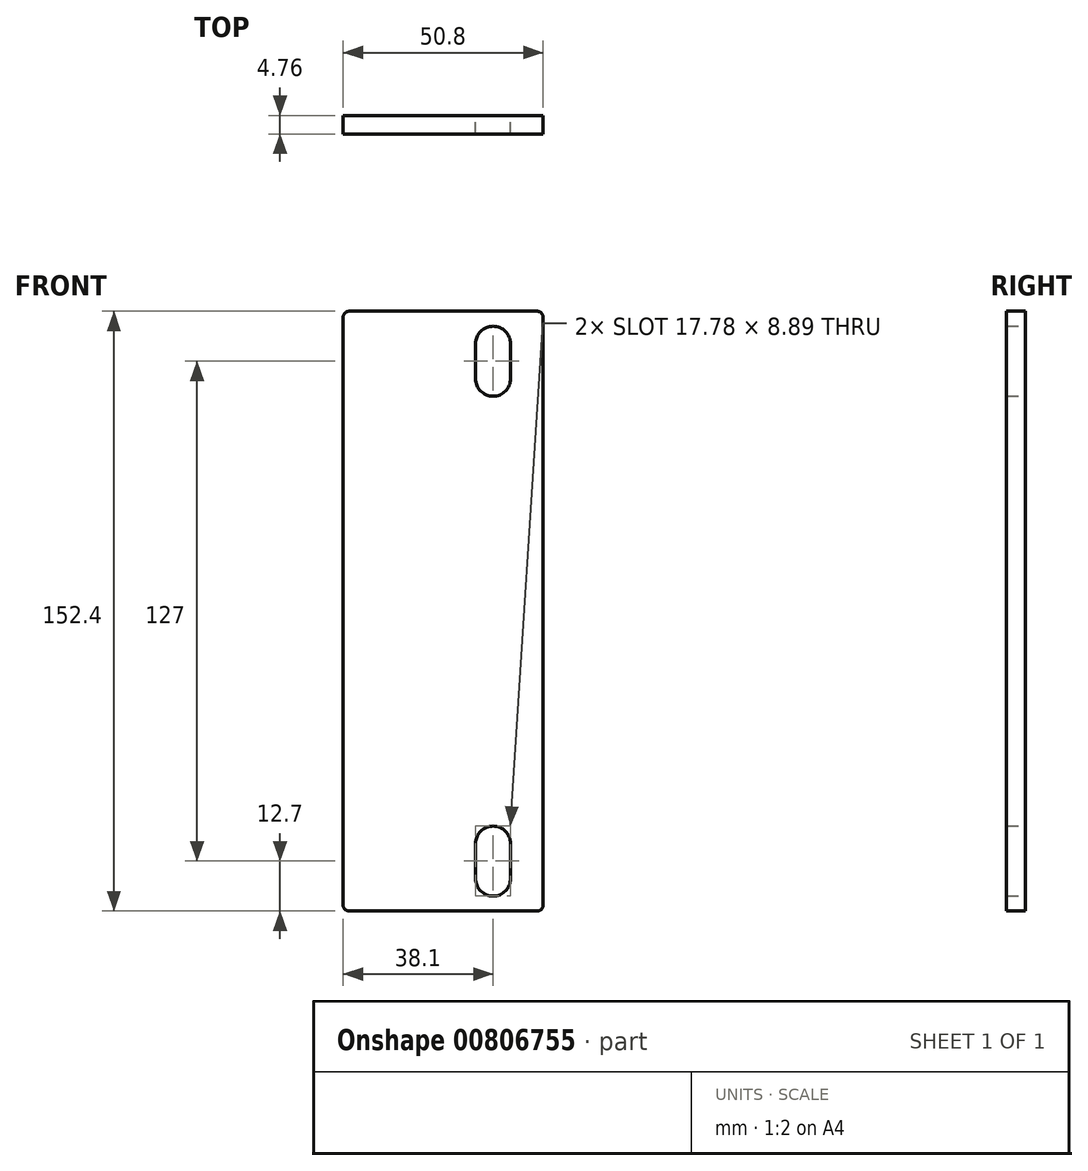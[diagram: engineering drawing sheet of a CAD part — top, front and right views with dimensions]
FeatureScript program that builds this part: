
annotation { "Feature Type Name" : "Feature", "Feature Type Description" : "" }
export const myFeature = defineFeature(function(context is Context, id is Id, definition is map)
    precondition{}
    {
        {
            var Q0;
            Q0=qCreatedBy(makeId("Front.planeOp"),FACE);
            var sketch = newSketch(context, id + "F0", { "sketchPlane" : qUnion([Q0])});
            skLineSegment(sketch, "E0.bottom", {"start": v(0, 1.52) * mm, "end": v(0, 150.88) * mm});
            skLineSegment(sketch, "E0.top", {"start": v(-50.8, 1.52) * mm, "end": v(-50.8, 150.88) * mm});
            skLineSegment(sketch, "E0.left", {"start": v(-1.52, 0) * mm, "end": v(-49.28, 0) * mm});
            skLineSegment(sketch, "E0.right", {"start": v(-1.52, 152.4) * mm, "end": v(-49.28, 152.4) * mm});
            skPoint(sketch, "E1.visualSharp", {"position": v(-50.8, 0) * mm});
            skArc(sketch, "E1.filletArc", {"start": v(-50.8, 1.52) * mm, "mid": v(-50.35, 0.45) * mm, "end": v(-49.28, 0) * mm});
            skPoint(sketch, "E2.visualSharp", {"position": v(0, 0) * mm});
            skArc(sketch, "E2.filletArc", {"start": v(-1.52, 0) * mm, "mid": v(-0.45, 0.45) * mm, "end": v(0, 1.52) * mm});
            skPoint(sketch, "E3.visualSharp", {"position": v(0, 152.4) * mm});
            skArc(sketch, "E3.filletArc", {"start": v(0, 150.88) * mm, "mid": v(-0.45, 151.95) * mm, "end": v(-1.52, 152.4) * mm});
            skPoint(sketch, "E4.visualSharp", {"position": v(-50.8, 152.4) * mm});
            skArc(sketch, "E4.filletArc", {"start": v(-49.28, 152.4) * mm, "mid": v(-50.35, 151.95) * mm, "end": v(-50.8, 150.88) * mm});
            skArc(sketch, "E5", {"start": v(-8.25, 144.15) * mm, "mid": v(-12.7, 148.6) * mm, "end": v(-17.14, 144.15) * mm});
            skArc(sketch, "E6", {"start": v(-17.14, 135.26) * mm, "mid": v(-12.7, 130.8) * mm, "end": v(-8.25, 135.26) * mm});
            skArc(sketch, "E7", {"start": v(-8.26, 17.15) * mm, "mid": v(-12.7, 21.6) * mm, "end": v(-17.14, 17.15) * mm});
            skArc(sketch, "E8", {"start": v(-17.14, 8.26) * mm, "mid": v(-12.7, 3.81) * mm, "end": v(-8.26, 8.26) * mm});
            skLineSegment(sketch, "E9", {"start": v(-17.14, 144.15) * mm, "end": v(-17.14, 135.26) * mm});
            skLineSegment(sketch, "E10", {"start": v(-8.25, 144.15) * mm, "end": v(-8.25, 135.26) * mm});
            skLineSegment(sketch, "E11", {"start": v(-8.26, 17.15) * mm, "end": v(-8.26, 8.26) * mm});
            skLineSegment(sketch, "E12", {"start": v(-17.14, 17.15) * mm, "end": v(-17.14, 8.26) * mm});
            skPoint(sketch, "E13.center.orphan", {"position": v(-12.7, 12.7) * mm});
            skPoint(sketch, "E14.center.orphan", {"position": v(-12.7, 139.7) * mm});
            skSolve(sketch);
        }
        {
            var Q0;
            Q0=makeQuery(id+"F0.imprint","IMPRINT",FACE,{"disambiguationData":[TD([[makeQuery(id+"F0.imprint","IMPRINT",EDGE,{"derivedFrom":sQuery(id+"F0.wireOp",EDGE,"E0.bottom")}),1.0]])]});
            extrude(context, id + "F1", {"entities" : qUnion([Q0]), "depth" : 4.76 * mm, "offsetDistance" : 25.4 * mm});
        }
    });
